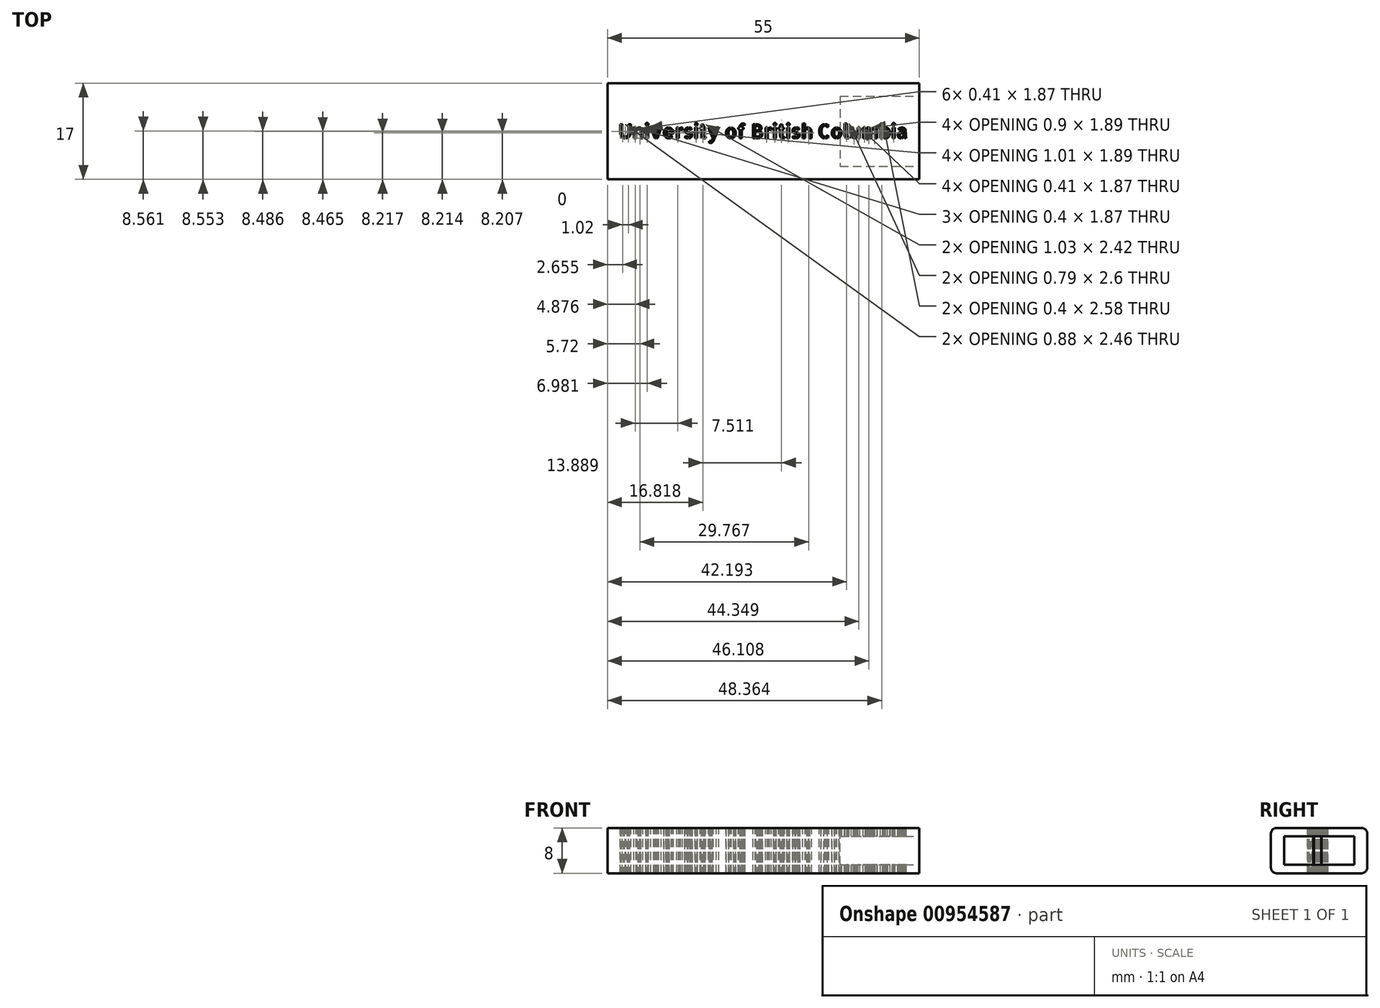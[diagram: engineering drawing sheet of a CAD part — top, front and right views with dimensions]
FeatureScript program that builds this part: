
annotation { "Feature Type Name" : "Feature", "Feature Type Description" : "" }
export const myFeature = defineFeature(function(context is Context, id is Id, definition is map)
    precondition{}
    {
        {
            var Q0;
            Q0=qCreatedBy(makeId("Front.planeOp"),FACE);
            var sketch = newSketch(context, id + "F0", { "sketchPlane" : qUnion([Q0])});
            skLineSegment(sketch, "E0.bottom", {"start": v(7.5, -4) * mm, "end": v(-7.5, -4) * mm});
            skLineSegment(sketch, "E0.top", {"start": v(7.5, 4) * mm, "end": v(-7.5, 4) * mm});
            skLineSegment(sketch, "E0.left", {"start": v(8.5, -3) * mm, "end": v(8.5, 3) * mm});
            skLineSegment(sketch, "E0.right", {"start": v(-8.5, -3) * mm, "end": v(-8.5, 3) * mm});
            skPoint(sketch, "E0.middle", {"position": v(0, 0) * mm});
            skPoint(sketch, "E1.visualSharp", {"position": v(-8.5, 4) * mm});
            skArc(sketch, "E1.filletArc", {"start": v(-7.5, 4) * mm, "mid": v(-8.2, 3.7) * mm, "end": v(-8.5, 3) * mm});
            skPoint(sketch, "E2.visualSharp", {"position": v(8.5, 4) * mm});
            skArc(sketch, "E2.filletArc", {"start": v(8.5, 3) * mm, "mid": v(8.2, 3.7) * mm, "end": v(7.5, 4) * mm});
            skPoint(sketch, "E3.visualSharp", {"position": v(8.5, -4) * mm});
            skArc(sketch, "E3.filletArc", {"start": v(7.5, -4) * mm, "mid": v(8.2, -3.7) * mm, "end": v(8.5, -3) * mm});
            skPoint(sketch, "E4.visualSharp", {"position": v(-8.5, -4) * mm});
            skArc(sketch, "E4.filletArc", {"start": v(-8.5, -3) * mm, "mid": v(-8.2, -3.7) * mm, "end": v(-7.5, -4) * mm});
            skSolve(sketch);
        }
        {
            var Q0;
            Q0 = qSketchRegion(id + "F0", true);
            extrude(context, id + "F1", {"entities" : qUnion([Q0]), "depth" : 55 * mm, "offsetDistance" : 25 * mm});
        }
        {
            var Q0;
            Q0=makeQuery(id+"F1.opExtrude","CAP_FACE",FACE,{"disambiguationData":[OSD([sQuery(id+"F0.wireOp",EDGE,"E0.bottom"),sQuery(id+"F0.wireOp",EDGE,"E0.top"),sQuery(id+"F0.wireOp",EDGE,"E0.left"),sQuery(id+"F0.wireOp",EDGE,"E0.right"),sQuery(id+"F0.wireOp",EDGE,"E1.filletArc"),sQuery(id+"F0.wireOp",EDGE,"E2.filletArc"),sQuery(id+"F0.wireOp",EDGE,"E3.filletArc"),sQuery(id+"F0.wireOp",EDGE,"E4.filletArc")])],"isStart":false});
            var sketch = newSketch(context, id + "F2", { "sketchPlane" : qUnion([Q0])});
            skLineSegment(sketch, "E5.bottom", {"start": v(6.2, -2.5) * mm, "end": v(-6.2, -2.5) * mm});
            skLineSegment(sketch, "E5.top", {"start": v(6.2, 2.5) * mm, "end": v(-6.2, 2.5) * mm});
            skLineSegment(sketch, "E5.left", {"start": v(6.2, -2.5) * mm, "end": v(6.2, 2.5) * mm});
            skLineSegment(sketch, "E5.right", {"start": v(-6.2, -2.5) * mm, "end": v(-6.2, 2.5) * mm});
            skPoint(sketch, "E5.middle", {"position": v(0, 0) * mm});
            skSolve(sketch);
        }
        {
            var Q0;
            Q0 = qSketchRegion(id + "F2", true);
            extrude(context, id + "F3", {"entities" : qUnion([Q0]), "operationType" : NewBodyOperationType.REMOVE, "oppositeDirection" : true, "depth" : 14 * mm, "offsetDistance" : 25 * mm});
        }
        {
            var Q0;
            Q0=makeQuery(id+"F1.opExtrude","SWEPT_BODY",BODY,{"disambiguationData":[OSD([sQuery(id+"F0.wireOp",EDGE,"E0.bottom"),sQuery(id+"F0.wireOp",EDGE,"E0.top"),sQuery(id+"F0.wireOp",EDGE,"E0.left"),sQuery(id+"F0.wireOp",EDGE,"E0.right"),sQuery(id+"F0.wireOp",EDGE,"E1.filletArc"),sQuery(id+"F0.wireOp",EDGE,"E2.filletArc"),sQuery(id+"F0.wireOp",EDGE,"E3.filletArc"),sQuery(id+"F0.wireOp",EDGE,"E4.filletArc")])]});
            var Q1;
            Q1=makeQuery(id+"F1.opExtrude","CAP_EDGE",EDGE,{"disambiguationData":[OSD([sQuery(id+"F0.wireOp",EDGE,"E0.left")])],"isStart":true});
            transform(context, id + "F4", {"entities" : qUnion([Q0]), "transformType" : TransformType.ROTATION, "transformAxis" : qUnion([Q1]), "angle" : 90 * degree, "makeCopy" : false});
        }
        {
            var Q0;
            Q0=makeQuery(id+"F1.opExtrude","SWEPT_FACE",FACE,{"disambiguationData":[OSD([sQuery(id+"F0.wireOp",EDGE,"E0.top")])]});
            var sketch = newSketch(context, id + "F5", { "sketchPlane" : qUnion([Q0])});
            skText(sketch, "E6", { "text": "University of British Columbia", "fontName": "AllertaStencil-Regular.ttf"});
            const initialGuessF5  = {"E6": [0.01044, -0.00973, 1, 0, 0.00245]};
            skSetInitialGuess(sketch, initialGuessF5);
            skSolve(sketch);
        }
        {
            var Q0;
            Q0 = qSketchRegion(id + "F5", true);
            extrude(context, id + "F6", {"entities" : qUnion([Q0]), "operationType" : NewBodyOperationType.REMOVE, "oppositeDirection" : true, "depth" : 25 * mm, "offsetDistance" : 25 * mm});
        }
    });
